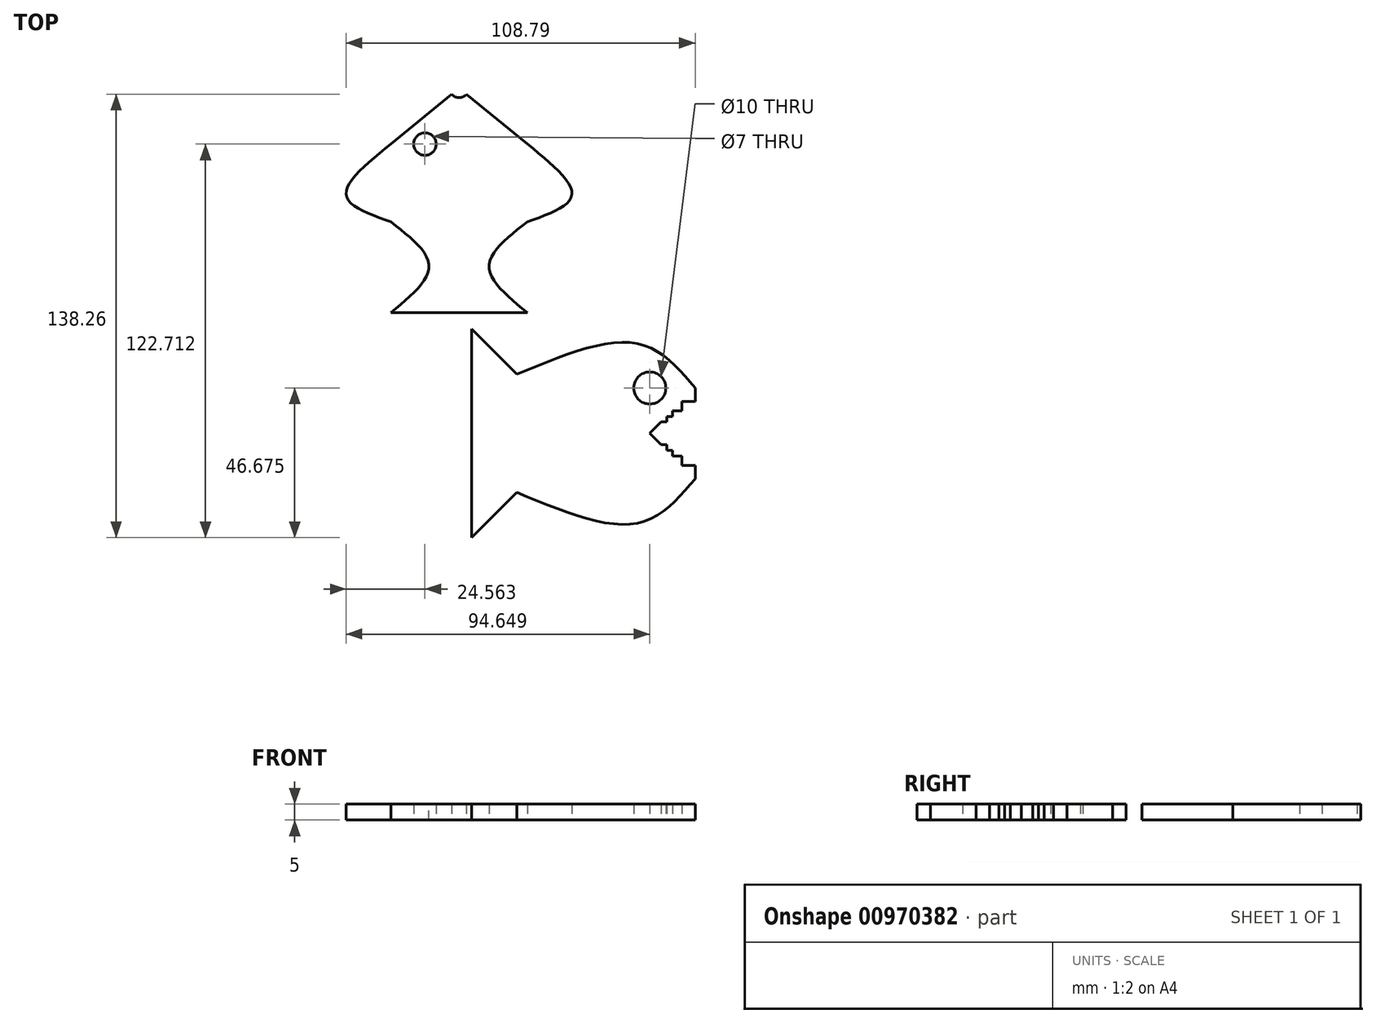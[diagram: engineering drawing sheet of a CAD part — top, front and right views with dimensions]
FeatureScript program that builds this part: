
annotation { "Feature Type Name" : "Feature", "Feature Type Description" : "" }
export const myFeature = defineFeature(function(context is Context, id is Id, definition is map)
    precondition{}
    {
        {
            var Q0;
            Q0=qCreatedBy(makeId("Top.planeOp"),FACE);
            var sketch = newSketch(context, id + "F0", { "sketchPlane" : qUnion([Q0])});
            skFitSpline(sketch, "E0", {"points": [v(0, 0) * mm, v(-11.88, 14.52) * mm, v(0, 28.3) * mm], "startDerivative": vector(-35.56, 29.09) * mm, "endDerivative": vector(35.74, 27.52) * mm});
            skFitSpline(sketch, "E1", {"points": [v(0, 28.3) * mm, v(13.88, 36.7) * mm, v(0, 52.57) * mm], "startDerivative": vector(42.74, 15.19) * mm, "endDerivative": vector(-40.91, 32.96) * mm});
            skFitSpline(sketch, "E2.MirrorCS", {"points": [v(-42.54, 0) * mm, v(-30.66, 14.52) * mm, v(-42.54, 28.3) * mm], "startDerivative": vector(35.56, 29.09) * mm, "endDerivative": vector(-35.74, 27.52) * mm});
            skFitSpline(sketch, "E3.MirrorCS", {"points": [v(-42.54, 28.3) * mm, v(-56.43, 36.7) * mm, v(-42.54, 52.57) * mm], "startDerivative": vector(-42.74, 15.19) * mm, "endDerivative": vector(40.91, 32.96) * mm});
            skLineSegment(sketch, "E4", {"start": v(-42.54, 52.57) * mm, "end": v(-23.6, 68.12) * mm});
            skLineSegment(sketch, "E5", {"start": v(-18.95, 68.12) * mm, "end": v(0, 52.57) * mm});
            skLineSegment(sketch, "E6", {"start": v(-42.54, 0) * mm, "end": v(0, 0) * mm});
            skPoint(sketch, "E7.endSnap0", {"position": v(-31.9, 61.3) * mm});
            skCircle(sketch, "E8", {"center": v(-31.9, 52.57) * mm, "radius": 3.5 * mm});
            skPoint(sketch, "E9.end.orphan", {"position": v(-21.27, 0) * mm});
            skArc(sketch, "E10", {"start": v(-23.6, 68.12) * mm, "mid": v(-21.27, 67.03) * mm, "end": v(-18.95, 68.12) * mm});
            skPoint(sketch, "E11", {"position": v(-23.6, 68.12) * mm});
            skPoint(sketch, "E12", {"position": v(-18.95, 68.12) * mm});
            skSolve(sketch);
        }
        {
            var Q0;
            Q0=makeQuery(id+"F0.imprint","IMPRINT",FACE,{"disambiguationData":[TD([[makeQuery(id+"F0.imprint","IMPRINT",EDGE,{"derivedFrom":sQuery(id+"F0.wireOp",EDGE,"E0")}),1.0]])]});
            extrude(context, id + "F1", {"entities" : qUnion([Q0]), "depth" : 5 * mm, "offsetDistance" : 25 * mm});
        }
        {
            var Q0;
            Q0=qCreatedBy(makeId("Top.planeOp"),FACE);
            var sketch = newSketch(context, id + "F2", { "sketchPlane" : qUnion([Q0])});
            skPoint(sketch, "E13.middle", {"position": v(43.18, -42.6) * mm});
            skLineSegment(sketch, "E14", {"start": v(38.18, -37.6) * mm, "end": v(52.32, -23.46) * mm});
            skLineSegment(sketch, "E15.MirrorCS", {"start": v(38.18, -37.6) * mm, "end": v(52.32, -51.75) * mm});
            skPoint(sketch, "E16.right.end.orphan", {"position": v(48.18, -27.6) * mm});
            skPoint(sketch, "E13.right.end.orphan", {"position": v(38.18, -47.6) * mm});
            skPoint(sketch, "E13.left.end.orphan", {"position": v(48.18, -47.6) * mm});
            skPoint(sketch, "E13.left.start.orphan", {"position": v(48.18, -37.6) * mm});
            skLineSegment(sketch, "E17", {"start": v(52.32, -23.46) * mm, "end": v(32.32, -23.46) * mm});
            skFitSpline(sketch, "E18", {"points": [v(52.32, -23.46) * mm, v(34.42, -9.64) * mm, v(-3.22, -19.21) * mm], "startDerivative": vector(-35.94, 42.52) * mm, "endDerivative": vector(-73.45, -30.74) * mm});
            skLineSegment(sketch, "E19", {"start": v(38.18, -37.6) * mm, "end": v(-3.22, -37.6) * mm});
            skFitSpline(sketch, "E20.MirrorCS", {"points": [v(52.32, -51.75) * mm, v(34.42, -65.58) * mm, v(-3.22, -56) * mm], "startDerivative": vector(-35.94, -42.52) * mm, "endDerivative": vector(-73.45, 30.74) * mm});
            skPoint(sketch, "E21.end.orphan", {"position": v(-18.67, 0) * mm});
            skPoint(sketch, "E22.end.orphan", {"position": v(-3.22, 0) * mm});
            skLineSegment(sketch, "E23", {"start": v(-3.22, -19.21) * mm, "end": v(-17.36, -5.07) * mm});
            skLineSegment(sketch, "E24.MirrorCS", {"start": v(-3.22, -56) * mm, "end": v(-17.36, -70.14) * mm});
            skLineSegment(sketch, "E25", {"start": v(-17.36, -5.07) * mm, "end": v(-17.36, -70.14) * mm});
            skLineSegment(sketch, "E26", {"start": v(52.32, -23.46) * mm, "end": v(48.18, -27.6) * mm});
            skLineSegment(sketch, "E27", {"start": v(48.18, -27.6) * mm, "end": v(52.32, -27.6) * mm});
            skLineSegment(sketch, "E28", {"start": v(52.32, -27.6) * mm, "end": v(52.32, -23.46) * mm});
            skLineSegment(sketch, "E29", {"start": v(48.18, -30.54) * mm, "end": v(45.25, -30.54) * mm});
            skPoint(sketch, "E29.startSnap0", {"position": v(45.25, -30.54) * mm});
            skLineSegment(sketch, "E30", {"start": v(48.18, -30.54) * mm, "end": v(48.18, -27.6) * mm});
            skLineSegment(sketch, "E31", {"start": v(45.25, -30.54) * mm, "end": v(38.18, -37.6) * mm});
            skLineSegment(sketch, "E32", {"start": v(41.71, -37.6) * mm, "end": v(38.18, -37.6) * mm});
            skPoint(sketch, "E32.startSnap0", {"position": v(41.71, -34.07) * mm});
            skLineSegment(sketch, "E33", {"start": v(41.71, -34.07) * mm, "end": v(41.71, -37.6) * mm});
            skLineSegment(sketch, "E34", {"start": v(41.71, -34.07) * mm, "end": v(45.25, -30.54) * mm});
            skLineSegment(sketch, "E35", {"start": v(45.25, -32.3) * mm, "end": v(45.25, -30.54) * mm});
            skPoint(sketch, "E35.startSnap0", {"position": v(43.48, -32.3) * mm});
            skLineSegment(sketch, "E36", {"start": v(43.48, -32.3) * mm, "end": v(45.25, -32.3) * mm});
            skLineSegment(sketch, "E37", {"start": v(43.48, -32.3) * mm, "end": v(41.71, -34.07) * mm});
            skLineSegment(sketch, "E38", {"start": v(43.48, -34.07) * mm, "end": v(43.48, -32.3) * mm});
            skLineSegment(sketch, "E39", {"start": v(41.71, -34.07) * mm, "end": v(43.48, -34.07) * mm});
            skLineSegment(sketch, "E40", {"start": v(38.18, -37.6) * mm, "end": v(52.32, -37.6) * mm});
            skLineSegment(sketch, "E41.MirrorCS", {"start": v(41.71, -41.14) * mm, "end": v(41.71, -37.6) * mm});
            skPoint(sketch, "E42.MirrorP", {"position": v(41.71, -41.14) * mm});
            skLineSegment(sketch, "E43.MirrorCS", {"start": v(41.71, -41.14) * mm, "end": v(43.48, -41.14) * mm});
            skLineSegment(sketch, "E44.MirrorCS", {"start": v(43.48, -41.14) * mm, "end": v(43.48, -42.91) * mm});
            skLineSegment(sketch, "E45.MirrorCS", {"start": v(45.25, -42.91) * mm, "end": v(45.25, -44.68) * mm});
            skLineSegment(sketch, "E46.MirrorCS", {"start": v(43.48, -42.91) * mm, "end": v(45.25, -42.91) * mm});
            skLineSegment(sketch, "E47.MirrorCS", {"start": v(48.18, -44.68) * mm, "end": v(45.25, -44.68) * mm});
            skLineSegment(sketch, "E48.MirrorCS", {"start": v(48.18, -44.68) * mm, "end": v(48.18, -47.6) * mm});
            skLineSegment(sketch, "E49.MirrorCS", {"start": v(48.18, -47.6) * mm, "end": v(52.32, -47.6) * mm});
            skLineSegment(sketch, "E50.MirrorCS", {"start": v(52.32, -47.6) * mm, "end": v(52.32, -51.75) * mm});
            skLineSegment(sketch, "E51", {"start": v(38.18, -37.6) * mm, "end": v(38.18, -23.46) * mm});
            skCircle(sketch, "E52", {"center": v(38.18, -23.46) * mm, "radius": 5 * mm});
            skSolve(sketch);
        }
        {
            var Q0;
            {var subQ0=sQuery(id+"F2.wireOp",EDGE,"E27");Q0=makeQuery(id+"F2.imprint","IMPRINT",FACE,{"disambiguationData":[TD([[makeQuery(id+"F2.imprint","IMPRINT",EDGE,{"derivedFrom":subQ0}),1.0]])]});}
            var Q1;
            {var subQ2=sQuery(id+"F2.wireOp",EDGE,"E29");Q1=makeQuery(id+"F2.imprint","IMPRINT",FACE,{"disambiguationData":[TD([[makeQuery(id+"F2.imprint","IMPRINT",EDGE,{"derivedFrom":subQ2}),-1.0]])]});}
            var Q2;
            {var subQ2=sQuery(id+"F2.wireOp",EDGE,"E35");Q2=makeQuery(id+"F2.imprint","IMPRINT",FACE,{"disambiguationData":[TD([[makeQuery(id+"F2.imprint","IMPRINT",EDGE,{"derivedFrom":subQ2}),1.0]])]});}
            var Q3;
            {var subQ0=sQuery(id+"F2.wireOp",EDGE,"E38");Q3=makeQuery(id+"F2.imprint","IMPRINT",FACE,{"disambiguationData":[TD([[makeQuery(id+"F2.imprint","IMPRINT",EDGE,{"derivedFrom":subQ0}),1.0]])]});}
            var Q4;
            {var subQ2=sQuery(id+"F2.wireOp",EDGE,"E45.MirrorCS");Q4=makeQuery(id+"F2.imprint","IMPRINT",FACE,{"disambiguationData":[TD([[makeQuery(id+"F2.imprint","IMPRINT",EDGE,{"derivedFrom":subQ2}),-1.0]])]});}
            var Q5;
            {var subQ2=sQuery(id+"F2.wireOp",EDGE,"E47.MirrorCS");Q5=makeQuery(id+"F2.imprint","IMPRINT",FACE,{"disambiguationData":[TD([[makeQuery(id+"F2.imprint","IMPRINT",EDGE,{"derivedFrom":subQ2}),1.0]])]});}
            var Q6;
            {var subQ0=sQuery(id+"F2.wireOp",EDGE,"E49.MirrorCS");Q6=makeQuery(id+"F2.imprint","IMPRINT",FACE,{"disambiguationData":[TD([[makeQuery(id+"F2.imprint","IMPRINT",EDGE,{"derivedFrom":subQ0}),-1.0]])]});}
            var Q7;
            {var subQ2=sQuery(id+"F2.wireOp",EDGE,"E43.MirrorCS");Q7=makeQuery(id+"F2.imprint","IMPRINT",FACE,{"disambiguationData":[TD([[makeQuery(id+"F2.imprint","IMPRINT",EDGE,{"derivedFrom":subQ2}),-1.0]])]});}
            var Q8;
            {var subQ7=sQuery(id+"F2.wireOp",EDGE,"E17");var subQ9=sQuery(id+"F2.wireOp",EDGE,"E52");var subQ11=makeQuery(id+"F2.imprint","INTERSECT",VERTEX,{"disambiguationData":[OD(1.0)],"derivedFrom":[subQ7,subQ9]});Q8=makeQuery(id+"F2.imprint","IMPRINT",FACE,{"disambiguationData":[TD([[makeQuery(id+"F2.imprint","IMPRINT",EDGE,{"disambiguationData":[TD([[subQ11,1.0]])],"derivedFrom":subQ9}),-1.0]])]});}
            var Q9;
            {var subQ7=sQuery(id+"F2.wireOp",EDGE,"E18");Q9=makeQuery(id+"F2.imprint","IMPRINT",FACE,{"disambiguationData":[TD([[makeQuery(id+"F2.imprint","IMPRINT",EDGE,{"derivedFrom":subQ7}),1.0]])]});}
            extrude(context, id + "F3", {"entities" : qUnion([Q0, Q1, Q2, Q3, Q4, Q5, Q6, Q7, Q8, Q9]), "depth" : 5 * mm, "offsetDistance" : 25 * mm});
        }
    });
